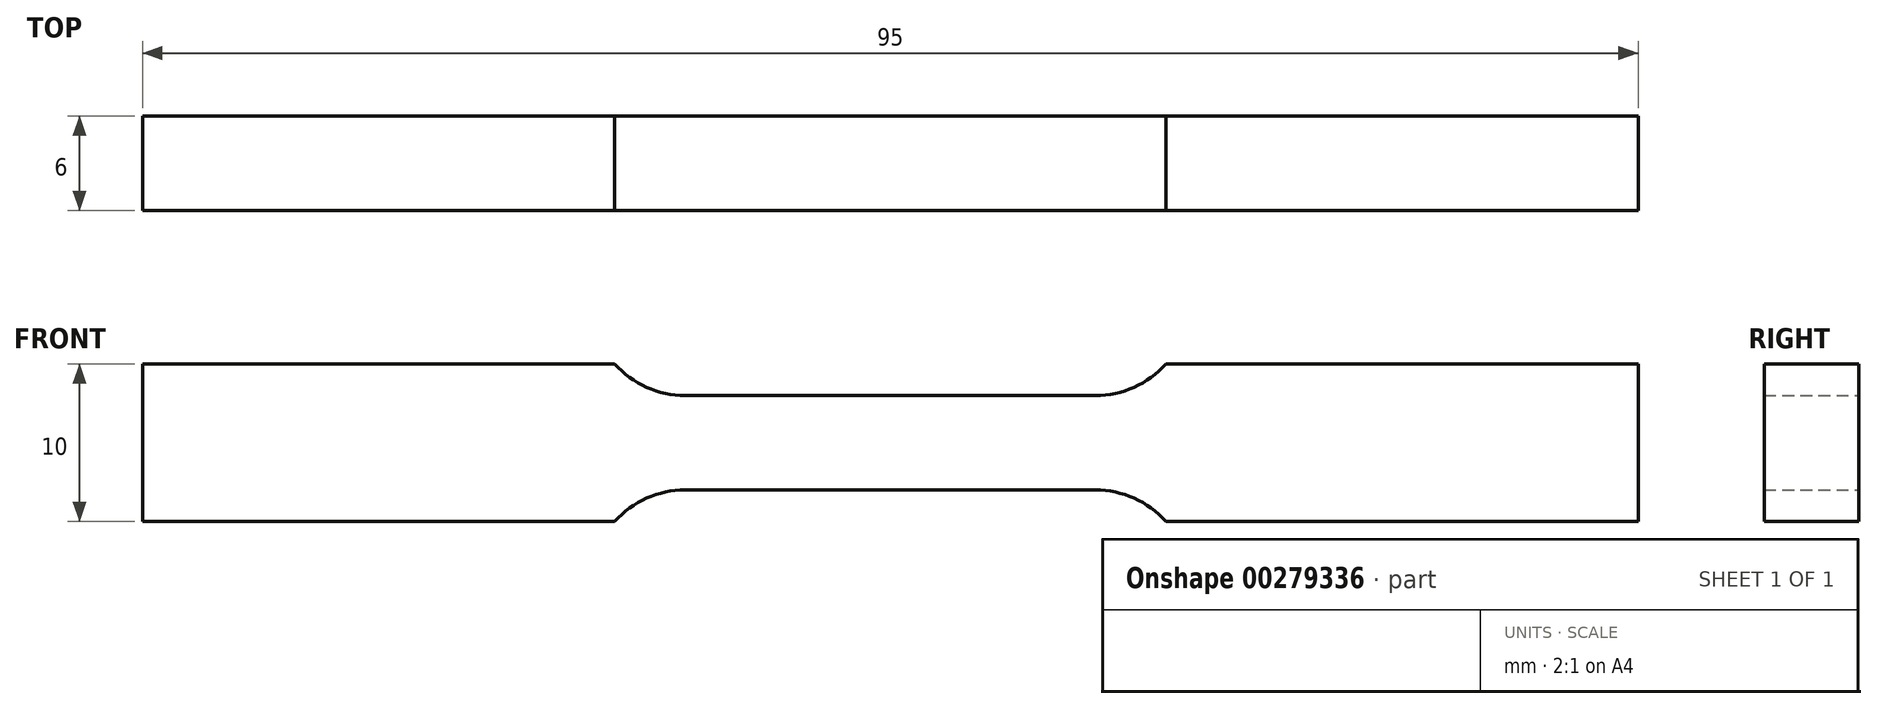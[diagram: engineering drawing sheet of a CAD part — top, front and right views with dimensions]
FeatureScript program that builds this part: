
annotation { "Feature Type Name" : "Feature", "Feature Type Description" : "" }
export const myFeature = defineFeature(function(context is Context, id is Id, definition is map)
    precondition{}
    {
        {
            var Q0;
            Q0=qCreatedBy(makeId("Front.planeOp"),FACE);
            var sketch = newSketch(context, id + "F0", { "sketchPlane" : qUnion([Q0])});
            skLineSegment(sketch, "E0", {"start": v(0, 3) * mm, "end": v(13.03, 3) * mm});
            skArc(sketch, "E1", {"start": v(13.03, 3) * mm, "mid": v(15.48, 3.52) * mm, "end": v(17.5, 5) * mm});
            skLineSegment(sketch, "E2", {"start": v(17.5, 5) * mm, "end": v(47.5, 5) * mm});
            skLineSegment(sketch, "E3", {"start": v(47.5, 5) * mm, "end": v(47.5, 0) * mm});
            skLineSegment(sketch, "E4.MirrorCS", {"start": v(0, -3) * mm, "end": v(13.03, -3) * mm});
            skLineSegment(sketch, "E5.MirrorCS", {"start": v(47.5, -5) * mm, "end": v(47.5, 0) * mm});
            skLineSegment(sketch, "E6.MirrorCS", {"start": v(17.5, -5) * mm, "end": v(47.5, -5) * mm});
            skArc(sketch, "E7.MirrorCS", {"start": v(13.03, -3) * mm, "mid": v(15.48, -3.52) * mm, "end": v(17.5, -5) * mm});
            skArc(sketch, "E8.MirrorCS", {"start": v(-13.03, -3) * mm, "mid": v(-15.48, -3.52) * mm, "end": v(-17.5, -5) * mm});
            skLineSegment(sketch, "E9.MirrorCS", {"start": v(-17.5, -5) * mm, "end": v(-47.5, -5) * mm});
            skLineSegment(sketch, "E10.MirrorCS", {"start": v(0, 3) * mm, "end": v(-13.03, 3) * mm});
            skArc(sketch, "E11.MirrorCS", {"start": v(-13.03, 3) * mm, "mid": v(-15.48, 3.52) * mm, "end": v(-17.5, 5) * mm});
            skLineSegment(sketch, "E12.MirrorCS", {"start": v(-17.5, 5) * mm, "end": v(-47.5, 5) * mm});
            skLineSegment(sketch, "E13.MirrorCS", {"start": v(-47.5, -5) * mm, "end": v(-47.5, 0) * mm});
            skLineSegment(sketch, "E14.MirrorCS", {"start": v(-47.5, 5) * mm, "end": v(-47.5, 0) * mm});
            skLineSegment(sketch, "E15.MirrorCS", {"start": v(0, -3) * mm, "end": v(-13.03, -3) * mm});
            skSolve(sketch);
        }
        {
            var Q0;
            Q0 = qSketchRegion(id + "F0", true);
            extrude(context, id + "F1", {"entities" : qUnion([Q0]), "endBound" : BoundingType.SYMMETRIC, "depth" : 6 * mm});
        }
    });
